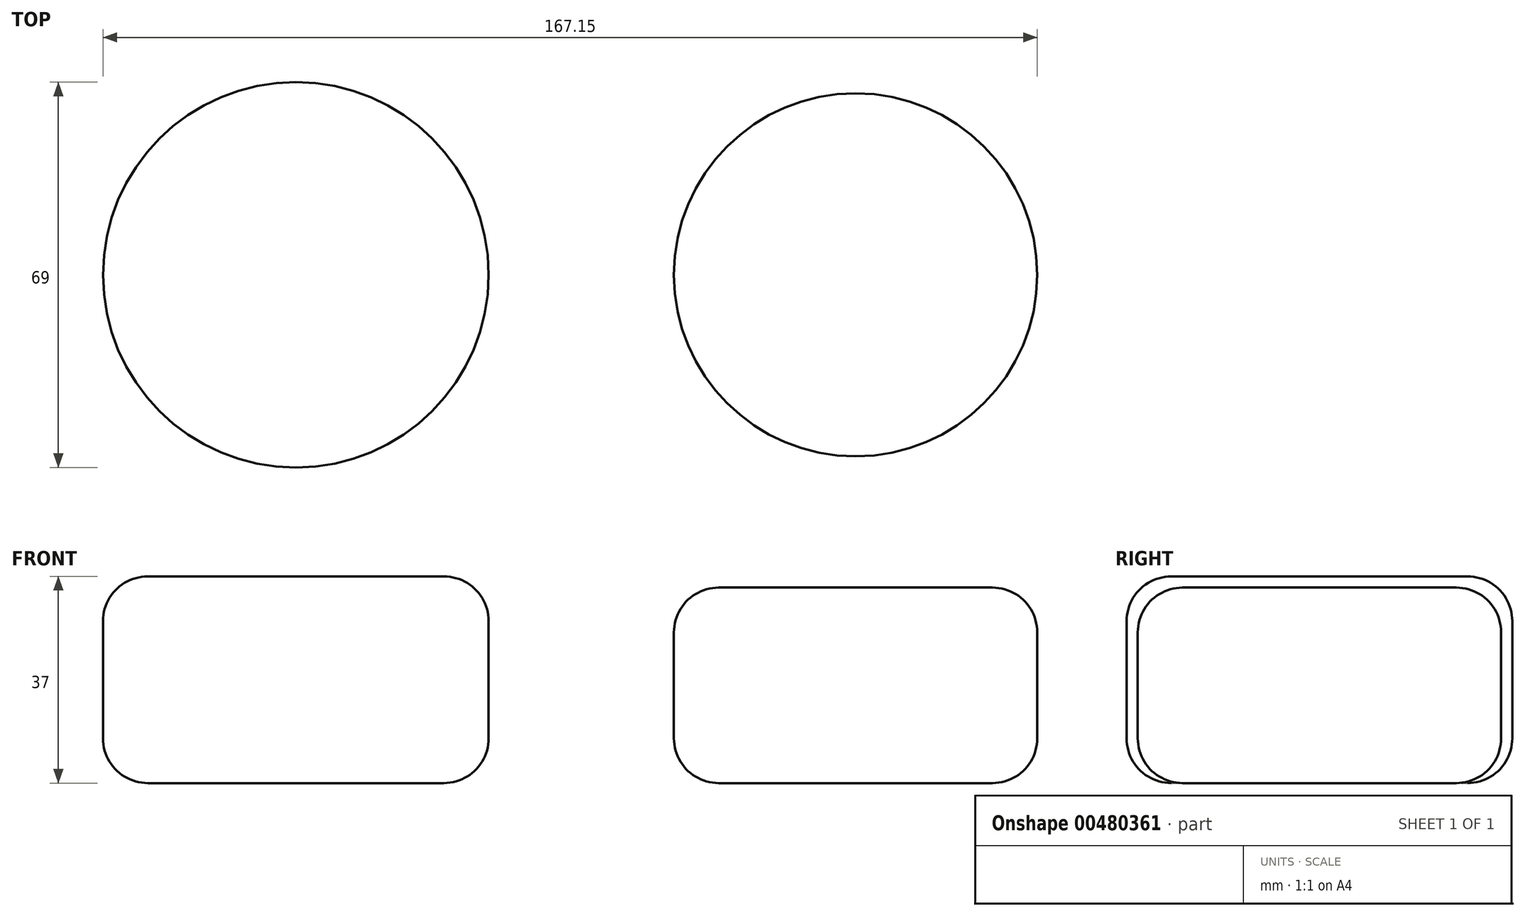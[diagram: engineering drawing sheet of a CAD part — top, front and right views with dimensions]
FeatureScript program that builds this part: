
annotation { "Feature Type Name" : "Feature", "Feature Type Description" : "" }
export const myFeature = defineFeature(function(context is Context, id is Id, definition is map)
    precondition{}
    {
        {
            var Q0;
            Q0=qCreatedBy(makeId("Top.planeOp"),FACE);
            var sketch = newSketch(context, id + "F0", { "sketchPlane" : qUnion([Q0])});
            skCircle(sketch, "E0", {"center": v(26.8, 0) * mm, "radius": 32.5 * mm});
            skCircle(sketch, "E1", {"center": v(-73.36, 0) * mm, "radius": 34.5 * mm});
            skSolve(sketch);
        }
        {
            var Q0;
            Q0=makeQuery(id+"F0.imprint","IMPRINT",FACE,{"disambiguationData":[TD([[makeQuery(id+"F0.imprint","IMPRINT",EDGE,{"derivedFrom":sQuery(id+"F0.wireOp",EDGE,"E1")}),1.0]])]});
            extrude(context, id + "F1", {"entities" : qUnion([Q0]), "depth" : 37 * mm, "offsetDistance" : 25 * mm});
        }
        {
            var Q0;
            Q0=makeQuery(id+"F0.imprint","IMPRINT",FACE,{"disambiguationData":[TD([[makeQuery(id+"F0.imprint","IMPRINT",EDGE,{"derivedFrom":sQuery(id+"F0.wireOp",EDGE,"E0")}),1.0]])]});
            extrude(context, id + "F2", {"entities" : qUnion([Q0]), "depth" : 35 * mm, "offsetDistance" : 25 * mm});
        }
        {
            var Q0;
            Q0=makeQuery(id+"F1.opExtrude","CAP_FACE",FACE,{"disambiguationData":[OSD([sQuery(id+"F0.wireOp",EDGE,"E1")])],"isStart":false});
            var Q1;
            Q1=makeQuery(id+"F1.opExtrude","CAP_FACE",FACE,{"disambiguationData":[OSD([sQuery(id+"F0.wireOp",EDGE,"E1")])],"isStart":true});
            var Q2;
            Q2=makeQuery(id+"F2.opExtrude","CAP_FACE",FACE,{"disambiguationData":[OSD([sQuery(id+"F0.wireOp",EDGE,"E0")])],"isStart":true});
            var Q3;
            Q3=makeQuery(id+"F2.opExtrude","CAP_FACE",FACE,{"disambiguationData":[OSD([sQuery(id+"F0.wireOp",EDGE,"E0")])],"isStart":false});
            fillet(context, id + "F3", {"entities" : qUnion([Q0, Q1, Q2, Q3]), "radius" : 8 * mm, "tangentPropagation" : true, "allowEdgeOverflow" : false});
        }
    });
